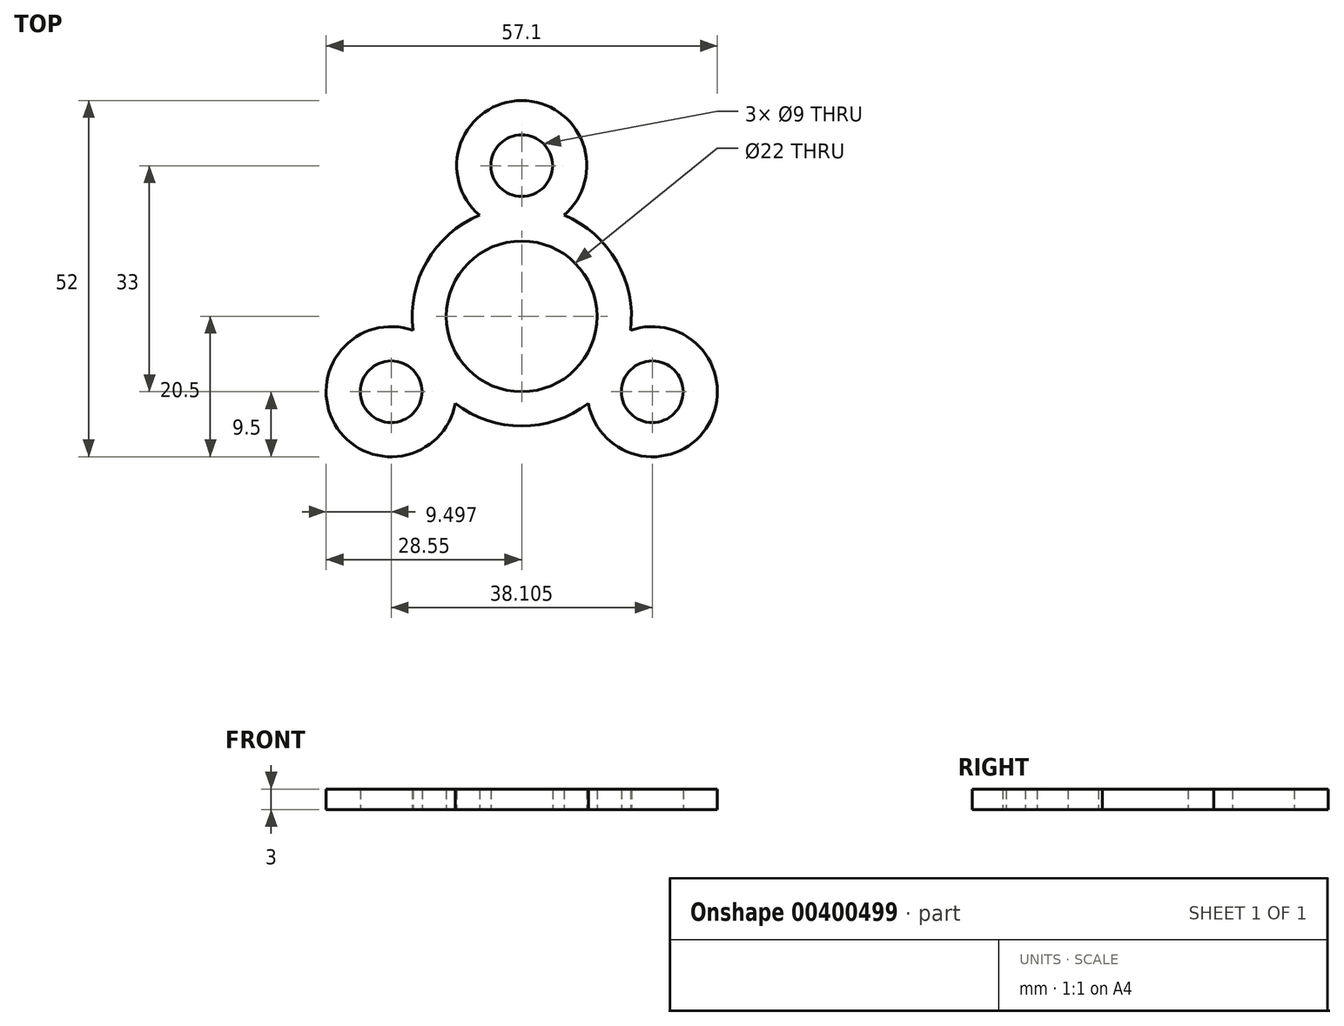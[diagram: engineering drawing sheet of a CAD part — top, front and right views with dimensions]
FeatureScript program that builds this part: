
annotation { "Feature Type Name" : "Feature", "Feature Type Description" : "" }
export const myFeature = defineFeature(function(context is Context, id is Id, definition is map)
    precondition{}
    {
        {
            var Q0;
            Q0=qCreatedBy(makeId("Top.planeOp"),FACE);
            var sketch = newSketch(context, id + "F0", { "sketchPlane" : qUnion([Q0])});
            skLineSegment(sketch, "E0", {"start": v(0, 0) * mm, "end": v(0, 22) * mm, "construction": true});
            skCircle(sketch, "E1", {"center": v(0, 22) * mm, "radius": 9.5 * mm});
            skCircle(sketch, "E2.1.0", {"center": v(-19.05, -11) * mm, "radius": 9.5 * mm});
            skCircle(sketch, "E2.2.0", {"center": v(19.05, -11) * mm, "radius": 9.5 * mm});
            skPoint(sketch, "E2.center", {"position": v(0, 0) * mm});
            skCircle(sketch, "E3.0", {"center": v(0, 0) * mm, "radius": 11 * mm});
            skCircle(sketch, "E4.0", {"center": v(0, 0) * mm, "radius": 16 * mm});
            skCircle(sketch, "E5.0", {"center": v(0, 22) * mm, "radius": 4.5 * mm});
            skCircle(sketch, "E6.1.0", {"center": v(-19.05, -11) * mm, "radius": 4.5 * mm});
            skCircle(sketch, "E6.2.0", {"center": v(19.05, -11) * mm, "radius": 4.5 * mm});
            skSolve(sketch);
        }
        {
            var Q0;
            Q0 = qSketchRegion(id + "F0", true);
            extrude(context, id + "F1", {"entities" : qUnion([Q0]), "depth" : 3 * mm});
        }
        {
            var Q0;
            Q0=makeQuery(id+"F1.opExtrude","SWEPT_BODY",BODY,{"disambiguationData":[OSD([sQuery(id+"F0.wireOp",EDGE,"E1"),sQuery(id+"F0.wireOp",EDGE,"E2.1.0"),sQuery(id+"F0.wireOp",EDGE,"E2.2.0"),sQuery(id+"F0.wireOp",EDGE,"E3.0"),sQuery(id+"F0.wireOp",EDGE,"E4.0"),sQuery(id+"F0.wireOp",EDGE,"E5.0"),sQuery(id+"F0.wireOp",EDGE,"E6.1.0"),sQuery(id+"F0.wireOp",EDGE,"E6.2.0")])]});
            transform(context, id + "F2", {"entities" : qUnion([Q0]), "transformType" : TransformType.TRANSLATION_3D, "dx" : 0 * mm, "dy" : 0 * mm, "dz" : 10 * mm, "makeCopy" : true});
        }
        {
            var Q0;
            Q0=makeQuery(id+"F2.opPattern","COPY",BODY,{"derivedFrom":makeQuery(id+"F1.opExtrude","SWEPT_BODY",BODY,{"disambiguationData":[OSD([sQuery(id+"F0.wireOp",EDGE,"E1"),sQuery(id+"F0.wireOp",EDGE,"E2.1.0"),sQuery(id+"F0.wireOp",EDGE,"E2.2.0"),sQuery(id+"F0.wireOp",EDGE,"E3.0"),sQuery(id+"F0.wireOp",EDGE,"E4.0"),sQuery(id+"F0.wireOp",EDGE,"E5.0"),sQuery(id+"F0.wireOp",EDGE,"E6.1.0"),sQuery(id+"F0.wireOp",EDGE,"E6.2.0")])]}),"instanceName":"1"});
            deleteBodies(context, id + "F3", {"entities" : qUnion([Q0])});
        }
    });
